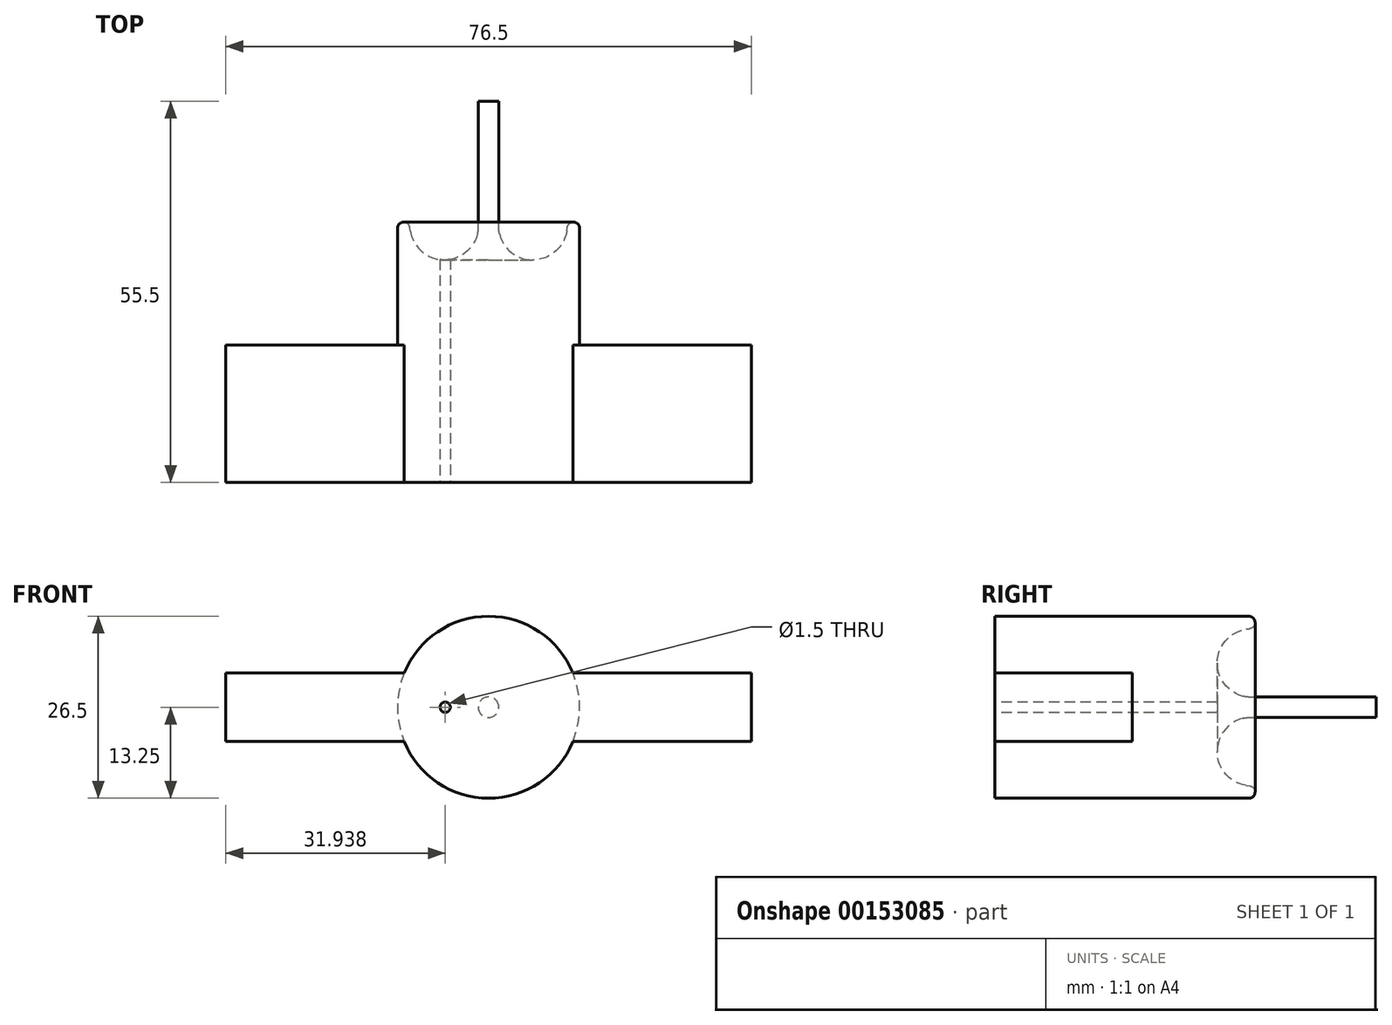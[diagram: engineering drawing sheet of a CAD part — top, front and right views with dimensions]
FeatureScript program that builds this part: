
annotation { "Feature Type Name" : "Feature", "Feature Type Description" : "" }
export const myFeature = defineFeature(function(context is Context, id is Id, definition is map)
    precondition{}
    {
        {
            var Q0;
            Q0=qCreatedBy(makeId("Top.planeOp"),FACE);
            var sketch = newSketch(context, id + "F0", { "sketchPlane" : qUnion([Q0])});
            skLineSegment(sketch, "E0", {"start": v(0, 0) * mm, "end": v(0, 8.99) * mm, "construction": true});
            skLineSegment(sketch, "E1", {"start": v(0, 0) * mm, "end": v(-13.25, 0) * mm});
            skLineSegment(sketch, "E2", {"start": v(-13.25, 0) * mm, "end": v(-13.25, 17) * mm});
            skArc(sketch, "E3", {"start": v(-11.38, 16.62) * mm, "mid": v(-6.44, 12.4) * mm, "end": v(-1.5, 16.62) * mm});
            skLineSegment(sketch, "E4", {"start": v(-1.5, 16.62) * mm, "end": v(-1.5, 37) * mm});
            skLineSegment(sketch, "E5", {"start": v(-1.5, 37) * mm, "end": v(0, 37) * mm});
            skLineSegment(sketch, "E6", {"start": v(0, 37) * mm, "end": v(0, 0) * mm});
            skArc(sketch, "E7", {"start": v(-11.46, 17.14) * mm, "mid": v(-12.42, 17.9) * mm, "end": v(-13.25, 17) * mm});
            skFitSpline(sketch, "E8", {"points": [v(-11.46, 17.14) * mm, v(-9.43, 12.3) * mm, v(-3.18, 12.17) * mm, v(-1.5, 16.62) * mm], "startDerivative": vector(0.25, -6.28) * mm, "endDerivative": vector(0.05, 11) * mm, "construction": true});
            skLineSegment(sketch, "E9", {"start": v(-11.46, 17.14) * mm, "end": v(-11.38, 16.62) * mm});
            skSolve(sketch);
        }
        {
            var Q0;
            Q0=makeQuery(id+"F0.imprint","IMPRINT",FACE,{"disambiguationData":[TD([[makeQuery(id+"F0.imprint","IMPRINT",EDGE,{"derivedFrom":sQuery(id+"F0.wireOp",EDGE,"E1")}),-1.0]])]});
            var Q1;
            Q1=sQuery(id+"F0.wireOp",EDGE,"E6");
            revolve(context, id + "F1", {"entities" : qUnion([Q0]), "axis" : qUnion([Q1]), "revolveType" : RevolveType.FULL});
        }
        {
            var Q0;
            Q0=makeQuery(id+"F1.opRevolve","SWEPT_EDGE",EDGE,{"disambiguationData":[OSD([sQuery(id+"F0.wireOp",EDGE,"E3"),sQuery(id+"F0.wireOp",EDGE,"E4")])]});
            fillet(context, id + "F2", {"entities" : qUnion([Q0]), "radius" : 3 * mm, "tangentPropagation" : true, "allowEdgeOverflow" : false});
        }
        {
            var Q0;
            Q0=makeQuery(id+"F1.opRevolve","SWEPT_FACE",FACE,{"disambiguationData":[OSD([sQuery(id+"F0.wireOp",EDGE,"E1")])]});
            var sketch = newSketch(context, id + "F3", { "sketchPlane" : qUnion([Q0])});
            skLineSegment(sketch, "E10.bottom", {"start": v(-38.25, 5) * mm, "end": v(38.25, 5) * mm});
            skLineSegment(sketch, "E10.top", {"start": v(-38.25, -5) * mm, "end": v(38.25, -5) * mm});
            skLineSegment(sketch, "E10.left", {"start": v(-38.25, 5) * mm, "end": v(-38.25, -5) * mm});
            skLineSegment(sketch, "E10.right", {"start": v(38.25, 5) * mm, "end": v(38.25, -5) * mm});
            skLineSegment(sketch, "E11", {"start": v(0, 0) * mm, "end": v(13.25, 0) * mm});
            skLineSegment(sketch, "E12", {"start": v(0, 0) * mm, "end": v(0, -3.36) * mm});
            skSolve(sketch);
        }
        {
            var Q0;
            {var subQ0=sQuery(id+"F3.wireOp",EDGE,"E10.left");Q0=makeQuery(id+"F3.imprint","IMPRINT",FACE,{"disambiguationData":[TD([[makeQuery(id+"F3.imprint","IMPRINT",EDGE,{"derivedFrom":subQ0}),1.0]])]});}
            var Q1;
            {var subQ4=sQuery(id+"F3.wireOp",EDGE,"E10.right");Q1=makeQuery(id+"F3.imprint","IMPRINT",FACE,{"disambiguationData":[TD([[makeQuery(id+"F3.imprint","IMPRINT",EDGE,{"derivedFrom":subQ4}),-1.0]])]});}
            var Q2;
            {var subQ0=makeQuery(id+"F1.opRevolve","SWEPT_EDGE",EDGE,{"disambiguationData":[OSD([sQuery(id+"F0.wireOp",EDGE,"E1"),sQuery(id+"F0.wireOp",EDGE,"E2")])]});var subQ3=makeQuery(id+"F3.imprint","IMPRINT",VERTEX,{"derivedFrom":subQ0});Q2=makeQuery(id+"F3.imprint","IMPRINT",FACE,{"disambiguationData":[TD([[makeQuery(id+"F3.imprint","IMPRINT",EDGE,{"disambiguationData":[TD([[subQ3,1.0]])],"derivedFrom":subQ0}),-1.0]])]});}
            extrude(context, id + "F4", {"entities" : qUnion([Q0, Q1, Q2]), "operationType" : NewBodyOperationType.ADD, "depth" : 20 * mm});
        }
        {
            var Q0;
            {var subQ0=sQuery(id+"F3.wireOp",EDGE,"E10.bottom");Q0=makeQuery(id+"F4.boolean.opBoolean","SPLIT",FACE,{"disambiguationData":[TD([makeQuery(id+"F4.opExtrude","SWEPT_FACE",FACE,{"disambiguationData":[OSD([subQ0])]})])],"derivedFrom":makeQuery(id+"F1.opRevolve","SWEPT_FACE",FACE,{"disambiguationData":[OSD([sQuery(id+"F0.wireOp",EDGE,"E1")])]})});}
            var Q1;
            {var subQ0=sQuery(id+"F3.wireOp",EDGE,"E10.top");Q1=makeQuery(id+"F4.boolean.opBoolean","SPLIT",FACE,{"disambiguationData":[TD([makeQuery(id+"F4.opExtrude","SWEPT_FACE",FACE,{"disambiguationData":[OSD([subQ0])]})])],"derivedFrom":makeQuery(id+"F1.opRevolve","SWEPT_FACE",FACE,{"disambiguationData":[OSD([sQuery(id+"F0.wireOp",EDGE,"E1")])]})});}
            extrude(context, id + "F5", {"entities" : qUnion([Q0, Q1]), "operationType" : NewBodyOperationType.ADD, "depth" : 20 * mm});
        }
        {
            var Q0;
            Q0=makeQuery(id+"F1.opRevolve","SWEPT_FACE",FACE,{"disambiguationData":[OSD([sQuery(id+"F0.wireOp",EDGE,"E5")])]});
            var sketch = newSketch(context, id + "F6", { "sketchPlane" : qUnion([Q0])});
            skCircle(sketch, "E13.0", {"center": v(0, 0) * mm, "radius": 1.5 * mm});
            skSolve(sketch);
        }
        {
            var Q0;
            Q0 = qSketchRegion(id + "F6", true);
            extrude(context, id + "F7", {"entities" : qUnion([Q0]), "operationType" : NewBodyOperationType.REMOVE, "oppositeDirection" : true, "depth" : 1.5 * mm});
        }
        {
            var Q0;
            {var subQ1=sQuery(id+"F3.wireOp",EDGE,"E10.right");var subQ2=sQuery(id+"F3.wireOp",EDGE,"E10.left");var subQ3=sQuery(id+"F3.wireOp",EDGE,"E10.top");var subQ4=sQuery(id+"F3.wireOp",EDGE,"E10.bottom");var subQ6=sQuery(id+"F0.wireOp",EDGE,"E1");var subQ7=makeQuery(id+"F1.opRevolve","SWEPT_FACE",FACE,{"disambiguationData":[OSD([subQ6])]});Q0=makeQuery(id+"F5.boolean.opBoolean","MERGE",FACE,{"derivedFrom":[makeQuery(id+"F4.opExtrude","CAP_FACE",FACE,{"disambiguationData":[OSD([subQ4,subQ3,subQ2,subQ1])],"isStart":false}),makeQuery(id+"F5.opExtrude","CAP_FACE",FACE,{"disambiguationData":[OSD([subQ6]),TDD([makeQuery(id+"F4.boolean.opBoolean","SPLIT",FACE,{"disambiguationData":[TD([makeQuery(id+"F4.opExtrude","SWEPT_FACE",FACE,{"disambiguationData":[OSD([subQ4])]})])],"derivedFrom":subQ7})])],"isStart":false}),makeQuery(id+"F5.opExtrude","CAP_FACE",FACE,{"disambiguationData":[OSD([subQ6]),TDD([makeQuery(id+"F4.boolean.opBoolean","SPLIT",FACE,{"disambiguationData":[TD([makeQuery(id+"F4.opExtrude","SWEPT_FACE",FACE,{"disambiguationData":[OSD([subQ3])]})])],"derivedFrom":subQ7})])],"isStart":false})]});}
            var sketch = newSketch(context, id + "F8", { "sketchPlane" : qUnion([Q0])});
            skCircle(sketch, "E14.0", {"center": v(0, 0) * mm, "radius": 1.5 * mm});
            skCircle(sketch, "E15.0", {"center": v(0, 0) * mm, "radius": 11.38 * mm});
            skCircle(sketch, "E16", {"center": v(-6.31, 0) * mm, "radius": 0.75 * mm});
            skSolve(sketch);
        }
        {
            var Q0;
            Q0=makeQuery(id+"F8.imprint","IMPRINT",FACE,{"disambiguationData":[TD([[makeQuery(id+"F8.imprint","IMPRINT",EDGE,{"derivedFrom":sQuery(id+"F8.wireOp",EDGE,"E16")}),1.0]])]});
            extrude(context, id + "F9", {"entities" : qUnion([Q0]), "operationType" : NewBodyOperationType.REMOVE, "endBound" : BoundingType.THROUGH_ALL, "oppositeDirection" : true, "depth" : 25 * mm});
        }
    });
